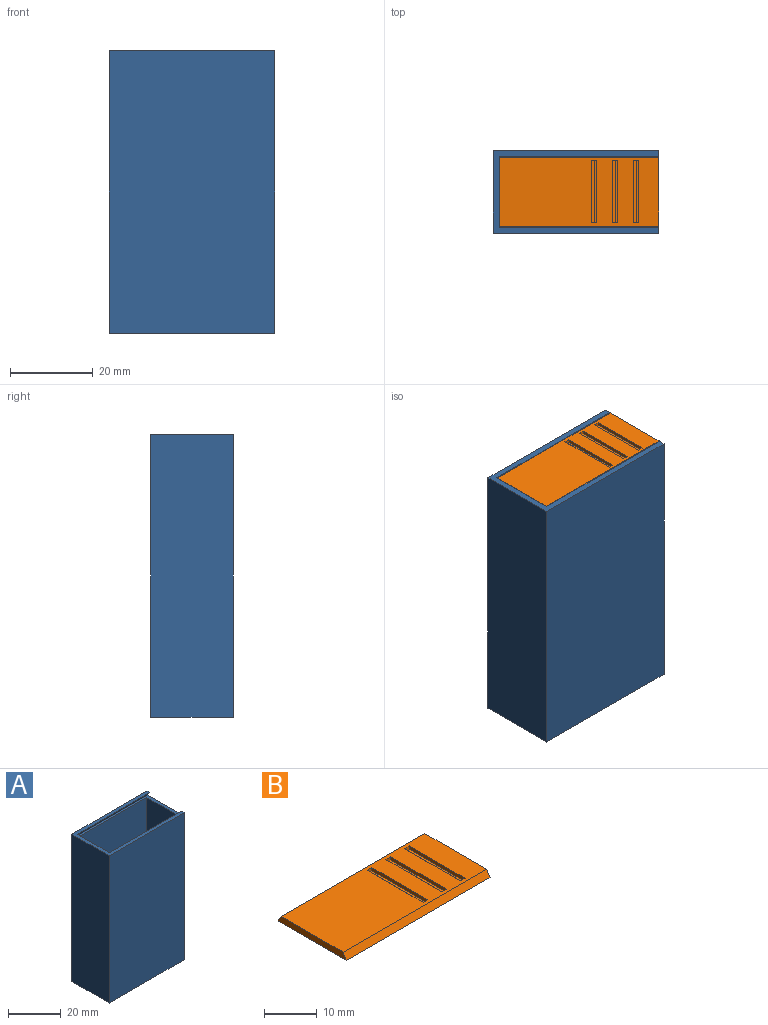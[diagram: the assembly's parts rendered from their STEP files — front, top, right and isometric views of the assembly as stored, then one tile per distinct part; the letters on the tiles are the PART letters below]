
ASSEMBLY  parts=2 mates=1
PART A: 14 faces, bbox 40x20x68 mm
  f0: plane 68x20mm, normal (1,0,0), area 1333.2mm2, adj f3,f5,f7,f8,f11,f12,f13
  f1: plane 65x37mm, normal (0,1,0), area 2405mm2, adj f6,f9,f10,f11
  f2: plane 65x37mm, normal (0,-1,0), area 2405mm2, adj f6,f9,f10,f11
  f3: plane 68x40mm, normal (0,1,0), area 2720mm2, adj f0,f4,f7,f8
  f4: plane 68x20mm, normal (-1,0,0), area 1360mm2, adj f3,f5,f7,f8
  f5: plane 68x40mm, normal (0,-1,0), area 2720mm2, adj f0,f4,f7,f8
  f6: plane 66.5x18.73mm, normal (1,0,0), area 1131.8mm2, adj f1,f2,f7,f9,f11,f12,f13
  f7: plane 40x20mm, normal (0,0,1), area 145.5mm2, adj f0,f3,f4,f5,f6,f12,f13
  f8: plane 40x20mm, normal (0,0,-1), area 800mm2, adj f0,f3,f4,f5
  f9: plane 37x17mm, normal (0,0,1), area 629mm2, adj f1,f2,f6,f10
  f10: plane 65x17mm, normal (-1,0,0), area 1105mm2, adj f1,f2,f9,f11
  f11: plane 38.5x18.73mm, normal (0,0,1), area 92.2mm2, adj f0,f1,f2,f6,f10,f12,f13
  f12: plane 38.5x1.5mm, normal (0,0.87,-0.5), area 66.7mm2, adj f0,f6,f7,f11
  f13: plane 38.5x1.5mm, normal (0,-0.87,-0.5), area 66.7mm2, adj f0,f6,f7,f11
PART B: 21 faces, bbox 38.5x18.3x1.5 mm
  f0: plane 38.5x16.6mm, normal (0,0,1), area 582.9mm2, adj f2,f3,f4,f5,f6,f7,f8,f10
  f1: plane 38.5x18.33mm, normal (0,0,-1), area 705.8mm2, adj f2,f3,f4,f5
  f2: plane 38.5x1.5mm, normal (0,0.87,0.5), area 66.7mm2, adj f0,f1,f4,f5
  f3: plane 38.5x1.5mm, normal (0,-0.87,0.5), area 66.7mm2, adj f0,f1,f4,f5
  f4: plane 18.33x1.5mm, normal (1,0,0), area 26.2mm2, adj f0,f1,f2,f3
  f5: plane 18.33x1.5mm, normal (-1,0,0), area 26.2mm2, adj f0,f1,f2,f3
  f6: plane 1.25x0.75mm, normal (0,-1,0), area 0.7mm2, adj f0,f8,f9,f20
  f7: plane 1.25x0.75mm, normal (0,1,0), area 0.7mm2, adj f0,f8,f9,f20
  f8: plane 15x0.75mm, normal (-1,0,0), area 11.3mm2, adj f0,f6,f7,f9
  f9: plane 15x0.5mm, normal (0,0,1), area 7.5mm2, adj f6,f7,f8,f20
  f10: plane 1.25x0.75mm, normal (0,-1,0), area 0.7mm2, adj f0,f12,f13,f19
  f11: plane 1.25x0.75mm, normal (0,1,0), area 0.7mm2, adj f0,f12,f13,f19
  f12: plane 15x0.75mm, normal (-1,0,0), area 11.3mm2, adj f0,f10,f11,f13
  f13: plane 15x0.5mm, normal (0,0,1), area 7.5mm2, adj f10,f11,f12,f19
  f14: plane 1.25x0.75mm, normal (0,-1,0), area 0.7mm2, adj f0,f16,f17,f18
  f15: plane 1.25x0.75mm, normal (0,1,0), area 0.7mm2, adj f0,f16,f17,f18
  f16: plane 15x0.75mm, normal (-1,0,0), area 11.3mm2, adj f0,f14,f15,f17
  f17: plane 15x0.5mm, normal (0,0,1), area 7.5mm2, adj f14,f15,f16,f18
  f18: plane 15x0.75mm, normal (0.71,0,0.71), area 15.9mm2, adj f0,f14,f15,f17
  f19: plane 15x0.75mm, normal (0.71,0,0.71), area 15.9mm2, adj f0,f10,f11,f13
  f20: plane 15x0.75mm, normal (0.71,0,0.71), area 15.9mm2, adj f0,f6,f7,f9
PLACE A t=(-20,-10,0)mm
PLACE B t=(-60,-10,66.5)mm
MATE slider B.f5 <-> A.f6  axis (-1,0,0) through (-18.5,0,68)mm
